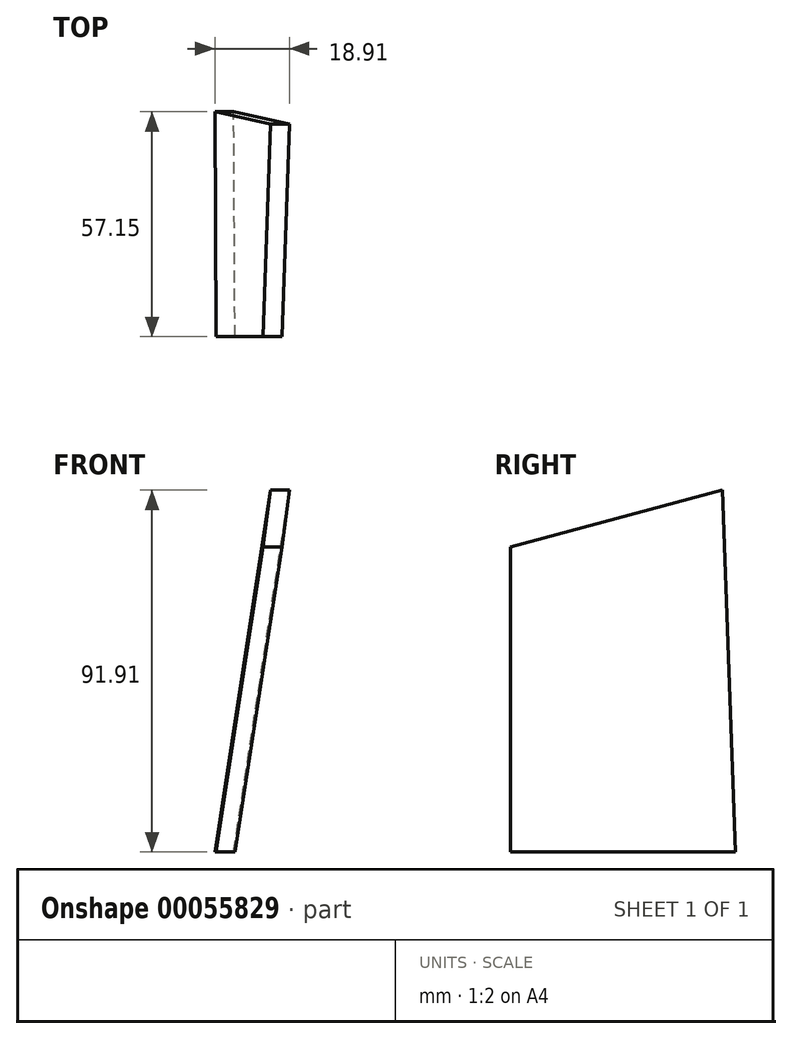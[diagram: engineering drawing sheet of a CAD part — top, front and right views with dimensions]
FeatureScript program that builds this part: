
annotation { "Feature Type Name" : "Feature", "Feature Type Description" : "" }
export const myFeature = defineFeature(function(context is Context, id is Id, definition is map)
    precondition{}
    {
        {
            var Q0;
            Q0=qCreatedBy(makeId("Front.planeOp"),FACE);
            var sketch = newSketch(context, id + "F0", { "sketchPlane" : qUnion([Q0])});
            skLineSegment(sketch, "E0", {"start": v(-28.55, 98.43) * mm, "end": v(28.55, 98.43) * mm, "construction": true});
            skLineSegment(sketch, "E1", {"start": v(-31.75, 98.43) * mm, "end": v(-43.84, 0) * mm});
            skLineSegment(sketch, "E2", {"start": v(31.75, 98.42) * mm, "end": v(43.84, 0) * mm, "construction": true});
            skLineSegment(sketch, "E3", {"start": v(-28.55, 98.43) * mm, "end": v(-29.04, 94.46) * mm, "construction": true});
            skLineSegment(sketch, "E4", {"start": v(29.04, 94.46) * mm, "end": v(28.55, 98.43) * mm, "construction": true});
            skLineSegment(sketch, "E5", {"start": v(-31.75, 98.43) * mm, "end": v(-28.55, 98.43) * mm, "construction": true});
            skLineSegment(sketch, "E6", {"start": v(28.55, 98.43) * mm, "end": v(31.75, 98.43) * mm, "construction": true});
            skLineSegment(sketch, "E7", {"start": v(-29.04, 94.46) * mm, "end": v(29.04, 94.46) * mm, "construction": true});
            skLineSegment(sketch, "E8", {"start": v(-28.55, 98.43) * mm, "end": v(-40.64, 0) * mm, "construction": true});
            skLineSegment(sketch, "E9", {"start": v(-31.75, 98.43) * mm, "end": v(31.75, 98.43) * mm});
            skLineSegment(sketch, "E10", {"start": v(40.64, 0) * mm, "end": v(29.04, 94.46) * mm, "construction": true});
            skLineSegment(sketch, "E11", {"start": v(31.75, 98.42) * mm, "end": v(43.84, 0) * mm});
            skLineSegment(sketch, "E12", {"start": v(-43.84, 0) * mm, "end": v(-36.67, 0) * mm});
            skLineSegment(sketch, "E13", {"start": v(-36.67, 0) * mm, "end": v(-22.98, 88.9) * mm});
            skLineSegment(sketch, "E14", {"start": v(-22.98, 88.9) * mm, "end": v(22.98, 88.9) * mm});
            skLineSegment(sketch, "E15", {"start": v(22.98, 88.9) * mm, "end": v(36.67, 0) * mm});
            skLineSegment(sketch, "E16", {"start": v(36.67, 0) * mm, "end": v(43.84, 0) * mm});
            skSolve(sketch);
        }
        {
            var Q0;
            Q0=qCreatedBy(makeId("Front.planeOp"),FACE);
            cPlane(context, id + "F1", {"entities" : qUnion([Q0]), "cplaneType" : CPlaneType.OFFSET, "offset" : 1.59 * mm, "width" : 152.4 * mm, "height" : 152.4 * mm});
        }
        {
            var Q0;
            Q0=qCreatedBy(id+"F1.planeOp",FACE);
            var sketch = newSketch(context, id + "F2", { "sketchPlane" : qUnion([Q0])});
            skLineSegment(sketch, "E17", {"start": v(0, 0) * mm, "end": v(-59.68, 0) * mm});
            skSolve(sketch);
        }
        {
            var Q0;
            Q0=sQuery(id+"F2.wireOp",EDGE,"E17");
            var Q1;
            Q1=qCreatedBy(id+"F1.planeOp",FACE);
            cPlane(context, id + "F3", {"entities" : qUnion([Q0, Q1]), "cplaneType" : CPlaneType.LINE_ANGLE, "offset" : 152.4 * mm, "angle" : 358 * degree, "width" : 152.4 * mm, "height" : 152.4 * mm});
        }
        {
            var Q0;
            Q0=qCreatedBy(id+"F3.planeOp",FACE);
            var sketch = newSketch(context, id + "F4", { "sketchPlane" : qUnion([Q0])});
            skLineSegment(sketch, "E18", {"start": v(-41.43, 0) * mm, "end": v(-27.07, 93.29) * mm});
            skLineSegment(sketch, "E19", {"start": v(-27.07, 93.29) * mm, "end": v(0, 93.29) * mm});
            skPoint(sketch, "E20.0", {"position": v(-36.67, 0) * mm});
            skLineSegment(sketch, "E21", {"start": v(-36.67, 0) * mm, "end": v(-41.43, 0) * mm});
            skLineSegment(sketch, "E22", {"start": v(-36.67, 0) * mm, "end": v(-23, 88.85) * mm});
            skLineSegment(sketch, "E23", {"start": v(-23, 88.85) * mm, "end": v(0, 88.85) * mm});
            skLineSegment(sketch, "E24", {"start": v(0, 0) * mm, "end": v(0, 97.14) * mm, "construction": true});
            skLineSegment(sketch, "E25.MirrorCS", {"start": v(36.67, 0) * mm, "end": v(41.43, 0) * mm});
            skLineSegment(sketch, "E26.MirrorCS", {"start": v(41.43, 0) * mm, "end": v(27.07, 93.29) * mm});
            skLineSegment(sketch, "E27.MirrorCS", {"start": v(36.67, 0) * mm, "end": v(23, 88.85) * mm});
            skLineSegment(sketch, "E28.MirrorCS", {"start": v(27.07, 93.29) * mm, "end": v(0, 93.29) * mm});
            skLineSegment(sketch, "E29.MirrorCS", {"start": v(23, 88.85) * mm, "end": v(0, 88.85) * mm});
            skSolve(sketch);
        }
        {
            var Q0;
            Q0=makeQuery(id+"F0.imprint","IMPRINT",FACE,{"disambiguationData":[TD([[makeQuery(id+"F0.imprint","IMPRINT",EDGE,{"derivedFrom":sQuery(id+"F0.wireOp",EDGE,"E1")}),1.0]])]});
            var Q1;
            Q1=makeQuery(id+"F4.imprint","IMPRINT",FACE,{"disambiguationData":[TD([[makeQuery(id+"F4.imprint","IMPRINT",EDGE,{"derivedFrom":sQuery(id+"F4.wireOp",EDGE,"E18")}),-1.0]])]});
            loft(context, id + "F5", {"sheetProfilesArray" : [{ "sheetProfileEntities" : qUnion([Q0]) }, { "sheetProfileEntities" : qUnion([Q1]) }]});
        }
        {
            var Q0;
            Q0=makeQuery(id+"F0.imprint","IMPRINT",FACE,{"disambiguationData":[TD([[makeQuery(id+"F0.imprint","IMPRINT",EDGE,{"derivedFrom":sQuery(id+"F0.wireOp",EDGE,"E1")}),1.0]])]});
            var sketch = newSketch(context, id + "F6", { "sketchPlane" : qUnion([Q0])});
            skLineSegment(sketch, "E30.0", {"start": v(-22.98, 88.9) * mm, "end": v(22.98, 88.9) * mm});
            skLineSegment(sketch, "E31.0", {"start": v(22.98, 88.9) * mm, "end": v(36.67, 0) * mm});
            skLineSegment(sketch, "E32.0", {"start": v(-36.67, 0) * mm, "end": v(-22.98, 88.9) * mm});
            skLineSegment(sketch, "E33", {"start": v(36.67, 0) * mm, "end": v(33.46, 0) * mm});
            skLineSegment(sketch, "E34", {"start": v(33.46, 0) * mm, "end": v(20.26, 85.73) * mm});
            skLineSegment(sketch, "E35", {"start": v(20.26, 85.73) * mm, "end": v(-20.26, 85.73) * mm});
            skLineSegment(sketch, "E36", {"start": v(-20.26, 85.73) * mm, "end": v(-33.46, 0) * mm});
            skLineSegment(sketch, "E37", {"start": v(-33.46, 0) * mm, "end": v(-36.67, 0) * mm});
            skSolve(sketch);
        }
        {
            var Q0;
            Q0=qSketchRegion(id+"F6",true);
            extrude(context, id + "F7", {"entities" : qUnion([Q0]), "operationType" : NewBodyOperationType.ADD, "depth" : 9.52 * mm});
        }
        {
            var Q0;
            Q0=qCreatedBy(makeId("Right.planeOp"),FACE);
            var sketch = newSketch(context, id + "F8", { "sketchPlane" : qUnion([Q0])});
            skPoint(sketch, "E38.0", {"position": v(-4.7, 88.9) * mm});
            skLineSegment(sketch, "E39.0", {"start": v(-9.53, 88.9) * mm, "end": v(-4.7, 88.9) * mm});
            skLineSegment(sketch, "E40", {"start": v(-4.7, 88.9) * mm, "end": v(-9.52, 88.05) * mm});
            skLineSegment(sketch, "E41", {"start": v(-9.52, 88.05) * mm, "end": v(-9.52, 88.9) * mm});
            skPoint(sketch, "E42.orphan", {"position": v(-9.53, 0) * mm});
            skSolve(sketch);
        }
        {
            var Q0;
            Q0=qSketchRegion(id+"F8",true);
            extrude(context, id + "F9", {"entities" : qUnion([Q0]), "operationType" : NewBodyOperationType.REMOVE, "endBound" : BoundingType.THROUGH_ALL, "oppositeDirection" : true, "depth" : 25.4 * mm, "hasSecondDirection" : true, "secondDirectionBound" : SecondDirectionBoundingType.THROUGH_ALL, "secondDirectionOppositeDirection" : false, "secondDirectionDepth" : 25.4 * mm});
        }
        {
            var Q0;
            Q0=makeQuery(id+"F5.opLoft","CAP_FACE",FACE,{"disambiguationData":[OSD([makeQuery(id+"F4.imprint","IMPRINT",FACE,{"disambiguationData":[TD([[makeQuery(id+"F4.imprint","IMPRINT",EDGE,{"derivedFrom":sQuery(id+"F4.wireOp",EDGE,"E18")}),-1.0]])]})])],"isStart":true});
            var sketch = newSketch(context, id + "F10", { "sketchPlane" : qUnion([Q0])});
            skFitSpline(sketch, "E43.0", {"points": [v(-27.07, 93.29) * mm, v(-31.86, 62.2) * mm, v(-36.64, 31.1) * mm, v(-41.43, 0) * mm]});
            skLineSegment(sketch, "E44", {"start": v(-41.43, 0) * mm, "end": v(-36.66, 0.06) * mm});
            skLineSegment(sketch, "E45", {"start": v(-36.66, 0.06) * mm, "end": v(-22.32, 93.29) * mm});
            skLineSegment(sketch, "E46", {"start": v(-22.32, 93.29) * mm, "end": v(-27.07, 93.29) * mm});
            skSolve(sketch);
        }
        {
            var Q0;
            Q0 = qSketchRegion(id + "F10", true);
            extrude(context, id + "F11", {"entities" : qUnion([Q0]), "depth" : 73.02 * mm});
        }
        {
            var Q0;
            Q0=qCreatedBy(makeId("Right.planeOp"),FACE);
            var sketch = newSketch(context, id + "F12", { "sketchPlane" : qUnion([Q0])});
            skFitSpline(sketch, "E47.0", {"points": [v(-77.82, 90.62) * mm, v(-53.5, 91.47) * mm, v(-29.17, 92.32) * mm, v(-4.84, 93.17) * mm]});
            skLineSegment(sketch, "E48", {"start": v(-4.8, 91.9) * mm, "end": v(-58.74, 77.46) * mm});
            skLineSegment(sketch, "E49", {"start": v(-77.82, 90.62) * mm, "end": v(-101.54, 90.62) * mm});
            skLineSegment(sketch, "E50", {"start": v(-101.54, 90.62) * mm, "end": v(-101.54, -8.14) * mm});
            skLineSegment(sketch, "E51", {"start": v(-101.54, -8.14) * mm, "end": v(0, -8.14) * mm});
            skLineSegment(sketch, "E52", {"start": v(0, -8.14) * mm, "end": v(0, 0) * mm});
            skLineSegment(sketch, "E53", {"start": v(0, 0) * mm, "end": v(-58.74, 0) * mm});
            skLineSegment(sketch, "E54", {"start": v(-58.74, 0) * mm, "end": v(-58.74, 77.46) * mm});
            skLineSegment(sketch, "E55.0", {"start": v(-9.52, 88.05) * mm, "end": v(-4.7, 88.9) * mm, "construction": true});
            skLineSegment(sketch, "E56", {"start": v(-4.84, 93.17) * mm, "end": v(-4.8, 91.9) * mm});
            skSolve(sketch);
        }
        {
            var Q0;
            Q0 = qSketchRegion(id + "F12", true);
            extrude(context, id + "F13", {"entities" : qUnion([Q0]), "operationType" : NewBodyOperationType.REMOVE, "endBound" : BoundingType.THROUGH_ALL, "oppositeDirection" : true, "depth" : 25.4 * mm});
        }
        {
            var Q0;
            Q0=makeQuery(id+"F5.opLoft","SWEPT_BODY",BODY,{"disambiguationData":[OSD([makeQuery(id+"F0.imprint","IMPRINT",FACE,{"disambiguationData":[TD([[makeQuery(id+"F0.imprint","IMPRINT",EDGE,{"derivedFrom":sQuery(id+"F0.wireOp",EDGE,"E1")}),1.0]])]}),makeQuery(id+"F4.imprint","IMPRINT",FACE,{"disambiguationData":[TD([[makeQuery(id+"F4.imprint","IMPRINT",EDGE,{"derivedFrom":sQuery(id+"F4.wireOp",EDGE,"E18")}),-1.0]])]})])]});
            deleteBodies(context, id + "F14", {"entities" : qUnion([Q0])});
        }
    });
